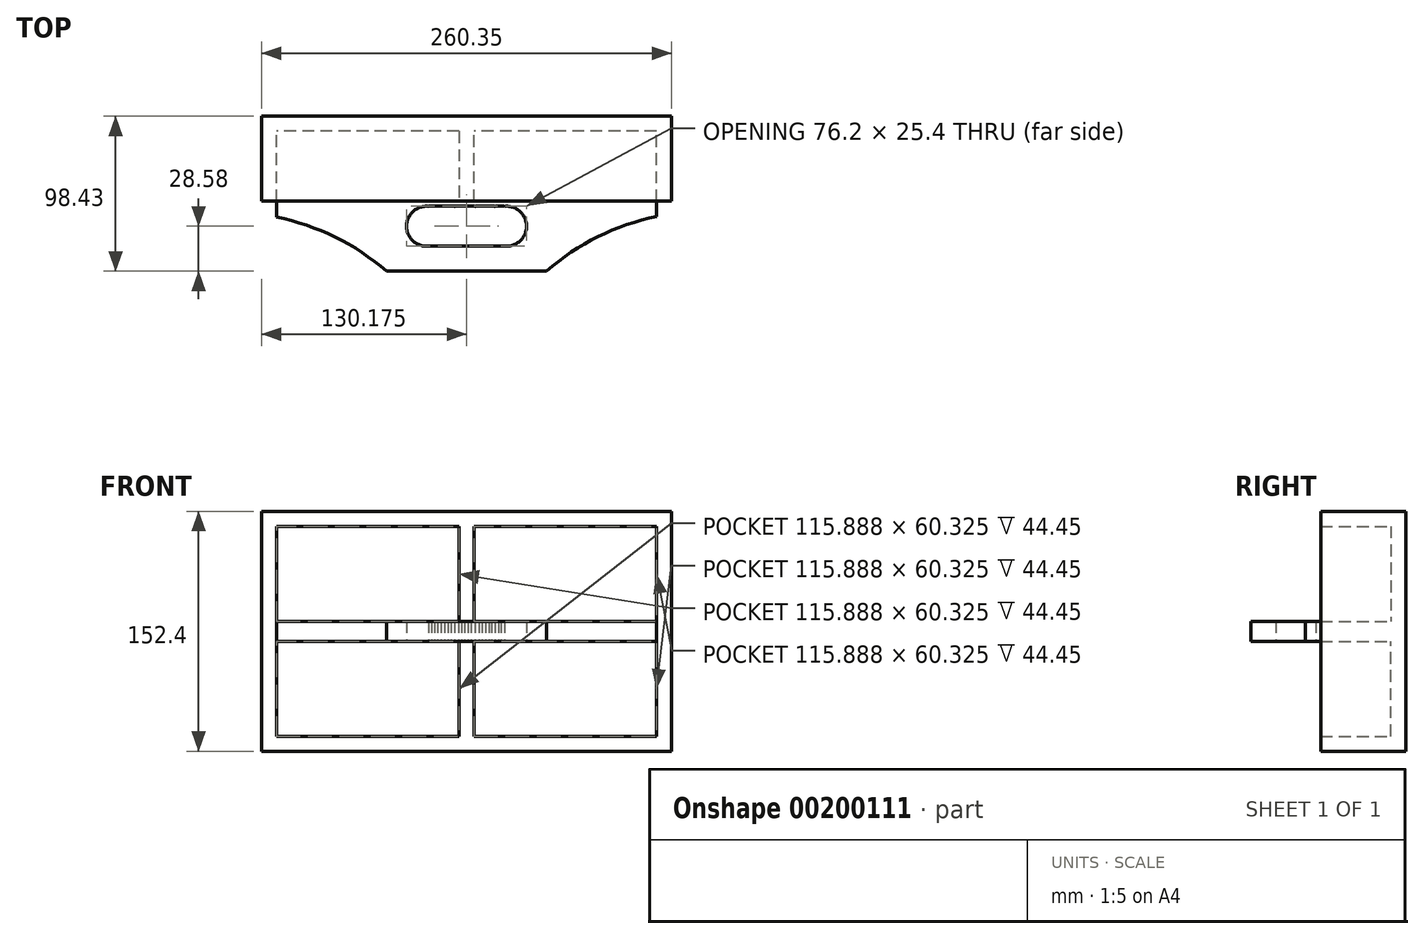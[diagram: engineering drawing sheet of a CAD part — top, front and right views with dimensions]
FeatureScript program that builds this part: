
annotation { "Feature Type Name" : "Feature", "Feature Type Description" : "" }
export const myFeature = defineFeature(function(context is Context, id is Id, definition is map)
    precondition{}
    {
        {
            var Q0;
            Q0=qCreatedBy(makeId("Front.planeOp"),FACE);
            var sketch = newSketch(context, id + "F0", { "sketchPlane" : qUnion([Q0])});
            skLineSegment(sketch, "E0", {"start": v(-126.24, -36.22) * mm, "end": v(134.1, -36.22) * mm});
            skLineSegment(sketch, "E1", {"start": v(134.1, -36.22) * mm, "end": v(134.1, 116.18) * mm});
            skLineSegment(sketch, "E2", {"start": v(134.1, 116.18) * mm, "end": v(-126.24, 116.18) * mm});
            skLineSegment(sketch, "E3", {"start": v(-126.24, -36.22) * mm, "end": v(-126.24, 116.18) * mm});
            skSolve(sketch);
        }
        {
            var Q0;
            Q0=makeQuery(id+"F0.imprint","IMPRINT",FACE,{"disambiguationData":[TD([[makeQuery(id+"F0.imprint","IMPRINT",EDGE,{"derivedFrom":sQuery(id+"F0.wireOp",EDGE,"E0")}),1.0]])]});
            extrude(context, id + "F1", {"entities" : qUnion([Q0]), "depth" : 9.52 * mm});
        }
        {
            var Q0;
            Q0=makeQuery(id+"F1.opExtrude","CAP_FACE",FACE,{"disambiguationData":[OSD([sQuery(id+"F0.wireOp",EDGE,"E0"),sQuery(id+"F0.wireOp",EDGE,"E1"),sQuery(id+"F0.wireOp",EDGE,"E2"),sQuery(id+"F0.wireOp",EDGE,"E3")])],"isStart":false});
            var sketch = newSketch(context, id + "F2", { "sketchPlane" : qUnion([Q0])});
            skLineSegment(sketch, "E4", {"start": v(134.1, -36.22) * mm, "end": v(134.1, -26.7) * mm});
            skLineSegment(sketch, "E5", {"start": v(-126.24, -36.22) * mm, "end": v(-126.24, -26.7) * mm});
            skLineSegment(sketch, "E6", {"start": v(-126.24, 116.18) * mm, "end": v(-126.24, 106.65) * mm});
            skLineSegment(sketch, "E7", {"start": v(134.1, 116.18) * mm, "end": v(134.1, 106.65) * mm});
            skLineSegment(sketch, "E8", {"start": v(-126.24, 106.65) * mm, "end": v(134.1, 106.65) * mm});
            skLineSegment(sketch, "E9", {"start": v(-126.24, -26.7) * mm, "end": v(134.1, -26.7) * mm});
            skLineSegment(sketch, "E10", {"start": v(124.58, 65.45) * mm, "end": v(124.58, 106.65) * mm});
            skLineSegment(sketch, "E11", {"start": v(124.58, 65.45) * mm, "end": v(124.58, -26.7) * mm});
            skLineSegment(sketch, "E12", {"start": v(-116.72, 49.02) * mm, "end": v(-116.72, 106.65) * mm});
            skLineSegment(sketch, "E13", {"start": v(-116.72, 49.02) * mm, "end": v(-116.72, -26.7) * mm});
            skLineSegment(sketch, "E14", {"start": v(-0.83, 77.84) * mm, "end": v(-0.83, 106.65) * mm});
            skLineSegment(sketch, "E15", {"start": v(-0.83, 77.84) * mm, "end": v(-0.83, -26.7) * mm});
            skLineSegment(sketch, "E16", {"start": v(8.7, 55.01) * mm, "end": v(8.7, 106.65) * mm});
            skLineSegment(sketch, "E17", {"start": v(8.7, 55.01) * mm, "end": v(8.7, -26.7) * mm});
            skPoint(sketch, "E18.start.orphan", {"position": v(-116.72, 77.84) * mm});
            skSolve(sketch);
        }
        {
            var Q0;
            {var subQ1=sQuery(id+"F2.wireOp",EDGE,"E12");Q0=makeQuery(id+"F2.imprint","IMPRINT",FACE,{"disambiguationData":[TD([[makeQuery(id+"F2.imprint","IMPRINT",EDGE,{"derivedFrom":subQ1}),1.0]])]});}
            var Q1;
            {var subQ3=sQuery(id+"F2.wireOp",EDGE,"E6");Q1=makeQuery(id+"F2.imprint","IMPRINT",FACE,{"disambiguationData":[TD([[makeQuery(id+"F2.imprint","IMPRINT",EDGE,{"derivedFrom":subQ3}),-1.0]])]});}
            var Q2;
            {var subQ1=sQuery(id+"F2.wireOp",EDGE,"E14");Q2=makeQuery(id+"F2.imprint","IMPRINT",FACE,{"disambiguationData":[TD([[makeQuery(id+"F2.imprint","IMPRINT",EDGE,{"derivedFrom":subQ1}),-1.0]])]});}
            var Q3;
            {var subQ1=sQuery(id+"F2.wireOp",EDGE,"E10");Q3=makeQuery(id+"F2.imprint","IMPRINT",FACE,{"disambiguationData":[TD([[makeQuery(id+"F2.imprint","IMPRINT",EDGE,{"derivedFrom":subQ1}),-1.0]])]});}
            var Q4;
            {var subQ4=sQuery(id+"F2.wireOp",EDGE,"E4");Q4=makeQuery(id+"F2.imprint","IMPRINT",FACE,{"disambiguationData":[TD([[makeQuery(id+"F2.imprint","IMPRINT",EDGE,{"derivedFrom":subQ4}),1.0]])]});}
            extrude(context, id + "F3", {"entities" : qUnion([Q0, Q1, Q2, Q3, Q4]), "operationType" : NewBodyOperationType.ADD, "depth" : 44.45 * mm});
        }
        {
            var Q0;
            {var subQ0=sQuery(id+"F2.wireOp",EDGE,"E10");var subQ3=sQuery(id+"F2.wireOp",EDGE,"E11");Q0=makeQuery(id+"F3.boolean.opBoolean","SPLIT",FACE,{"disambiguationData":[TD([makeQuery(id+"F3.opExtrude","SWEPT_FACE",FACE,{"disambiguationData":[OSD([subQ0,subQ3])]})])],"derivedFrom":makeQuery(id+"F1.opExtrude","CAP_FACE",FACE,{"disambiguationData":[OSD([sQuery(id+"F0.wireOp",EDGE,"E0"),sQuery(id+"F0.wireOp",EDGE,"E1"),sQuery(id+"F0.wireOp",EDGE,"E2"),sQuery(id+"F0.wireOp",EDGE,"E3")])],"isStart":false})});}
            var sketch = newSketch(context, id + "F4", { "sketchPlane" : qUnion([Q0])});
            skPoint(sketch, "E19.end.orphan", {"position": v(-116.72, 35.97) * mm});
            skPoint(sketch, "E19.start.orphan", {"position": v(124.58, 35.97) * mm});
            skLineSegment(sketch, "E20", {"start": v(38.58, 33.63) * mm, "end": v(124.58, 33.63) * mm});
            skLineSegment(sketch, "E21", {"start": v(38.58, 33.63) * mm, "end": v(-116.72, 33.63) * mm});
            skLineSegment(sketch, "E22", {"start": v(37.81, 46.33) * mm, "end": v(124.58, 46.33) * mm});
            skLineSegment(sketch, "E23", {"start": v(-4.04, 46.33) * mm, "end": v(-116.72, 46.33) * mm});
            skPoint(sketch, "E24", {"position": v(-4.04, 46.33) * mm});
            skLineSegment(sketch, "E25", {"start": v(-116.72, 46.33) * mm, "end": v(-116.72, 33.63) * mm});
            skLineSegment(sketch, "E26", {"start": v(124.58, 33.63) * mm, "end": v(124.58, 46.33) * mm});
            skLineSegment(sketch, "E27", {"start": v(37.81, 46.33) * mm, "end": v(-4.04, 46.33) * mm});
            skSolve(sketch);
        }
        {
            var Q0;
            {var subQ1=sQuery(id+"F4.wireOp",EDGE,"E23");Q0=makeQuery(id+"F4.imprint","IMPRINT",FACE,{"disambiguationData":[TD([[makeQuery(id+"F4.imprint","IMPRINT",EDGE,{"derivedFrom":subQ1}),1.0]])]});}
            var Q1;
            {var subQ2=sQuery(id+"F4.wireOp",EDGE,"E20");Q1=makeQuery(id+"F4.imprint","IMPRINT",FACE,{"disambiguationData":[TD([[makeQuery(id+"F4.imprint","IMPRINT",EDGE,{"derivedFrom":subQ2}),1.0]])]});}
            extrude(context, id + "F5", {"entities" : qUnion([Q0, Q1]), "operationType" : NewBodyOperationType.ADD, "depth" : 88.9 * mm});
        }
        {
            var Q0;
            Q0=makeQuery(id+"F5.opExtrude","SWEPT_FACE",FACE,{"disambiguationData":[OSD([sQuery(id+"F4.wireOp",EDGE,"E20"),sQuery(id+"F4.wireOp",EDGE,"E21")])]});
            var sketch = newSketch(context, id + "F6", { "sketchPlane" : qUnion([Q0])});
            skLineSegment(sketch, "E28", {"start": v(-47.37, 98.43) * mm, "end": v(-21.47, 98.43) * mm});
            skLineSegment(sketch, "E29", {"start": v(54.73, 98.43) * mm, "end": v(29.33, 98.43) * mm});
            skPoint(sketch, "E30.end.orphan", {"position": v(29.33, 69.85) * mm});
            skPoint(sketch, "E30.start.orphan", {"position": v(29.33, 96.52) * mm});
            skLineSegment(sketch, "E31", {"start": v(29.33, 98.43) * mm, "end": v(29.33, 96.52) * mm});
            skArc(sketch, "E32", {"start": v(-21.47, 82.55) * mm, "mid": v(-34.17, 69.85) * mm, "end": v(-21.47, 57.15) * mm});
            skArc(sketch, "E33", {"start": v(29.33, 57.15) * mm, "mid": v(42.03, 69.85) * mm, "end": v(29.33, 82.55) * mm});
            skLineSegment(sketch, "E34", {"start": v(-21.47, 57.15) * mm, "end": v(29.33, 57.15) * mm});
            skLineSegment(sketch, "E35", {"start": v(29.33, 82.55) * mm, "end": v(-21.47, 82.55) * mm});
            skArc(sketch, "E36", {"start": v(-116.72, 63.5) * mm, "mid": v(-79.78, 76.47) * mm, "end": v(-47.37, 98.42) * mm});
            skArc(sketch, "E37", {"start": v(54.73, 98.43) * mm, "mid": v(87.42, 76.64) * mm, "end": v(124.58, 63.94) * mm});
            skLineSegment(sketch, "E38", {"start": v(-21.47, 69.85) * mm, "end": v(29.33, 69.85) * mm});
            skPoint(sketch, "E39", {"position": v(-19.25, 69.85) * mm});
            skPoint(sketch, "E40", {"position": v(-17.28, 69.85) * mm});
            skPoint(sketch, "E41", {"position": v(-15.5, 69.85) * mm});
            skPoint(sketch, "E42", {"position": v(-13.25, 69.85) * mm});
            skPoint(sketch, "E43", {"position": v(-11.23, 69.85) * mm});
            skPoint(sketch, "E44", {"position": v(-8.84, 69.85) * mm});
            skPoint(sketch, "E45", {"position": v(-6.77, 69.85) * mm});
            skPoint(sketch, "E46", {"position": v(-4.8, 69.85) * mm});
            skPoint(sketch, "E47", {"position": v(-2.3, 69.85) * mm});
            skPoint(sketch, "E48", {"position": v(-0.29, 69.85) * mm});
            skPoint(sketch, "E49", {"position": v(1.63, 69.85) * mm});
            skPoint(sketch, "E50", {"position": v(3.93, 69.85) * mm});
            skPoint(sketch, "E51", {"position": v(5.8, 69.85) * mm});
            skPoint(sketch, "E52", {"position": v(8.06, 69.85) * mm});
            skPoint(sketch, "E53", {"position": v(10.69, 69.85) * mm});
            skPoint(sketch, "E54", {"position": v(12.84, 69.85) * mm});
            skPoint(sketch, "E55", {"position": v(14.86, 69.85) * mm});
            skPoint(sketch, "E56", {"position": v(17.06, 69.85) * mm});
            skPoint(sketch, "E57", {"position": v(19.22, 69.85) * mm});
            skPoint(sketch, "E58", {"position": v(20.68, 69.85) * mm});
            skPoint(sketch, "E59", {"position": v(23.26, 69.85) * mm});
            skPoint(sketch, "E60", {"position": v(25.04, 69.85) * mm});
            skPoint(sketch, "E61", {"position": v(26.87, 69.85) * mm});
            skSolve(sketch);
        }
        {
            var Q0;
            Q0=sQuery(id+"F6.wireOp",VERTEX,"E38.start");
            var Q1;
            Q1=sQuery(id+"F6.wireOp",VERTEX,"E39");
            var Q2;
            Q2=sQuery(id+"F6.wireOp",VERTEX,"E40");
            var Q3;
            Q3=sQuery(id+"F6.wireOp",VERTEX,"E41");
            var Q4;
            Q4=sQuery(id+"F6.wireOp",VERTEX,"E42");
            var Q5;
            Q5=sQuery(id+"F6.wireOp",VERTEX,"E43");
            var Q6;
            Q6=sQuery(id+"F6.wireOp",VERTEX,"E44");
            var Q7;
            Q7=sQuery(id+"F6.wireOp",VERTEX,"E45");
            var Q8;
            Q8=sQuery(id+"F6.wireOp",VERTEX,"E46");
            var Q9;
            Q9=sQuery(id+"F6.wireOp",VERTEX,"E47");
            var Q10;
            Q10=sQuery(id+"F6.wireOp",VERTEX,"E48");
            var Q11;
            Q11=sQuery(id+"F6.wireOp",VERTEX,"E49");
            var Q12;
            Q12=sQuery(id+"F6.wireOp",VERTEX,"E50");
            var Q13;
            Q13=sQuery(id+"F6.wireOp",VERTEX,"E51");
            var Q14;
            Q14=sQuery(id+"F6.wireOp",VERTEX,"E52");
            var Q15;
            Q15=sQuery(id+"F6.wireOp",VERTEX,"E53");
            var Q16;
            Q16=sQuery(id+"F6.wireOp",VERTEX,"E54");
            var Q17;
            Q17=sQuery(id+"F6.wireOp",VERTEX,"E55");
            var Q18;
            Q18=sQuery(id+"F6.wireOp",VERTEX,"E56");
            var Q19;
            Q19=sQuery(id+"F6.wireOp",VERTEX,"E57");
            var Q20;
            Q20=sQuery(id+"F6.wireOp",VERTEX,"E58");
            var Q21;
            Q21=sQuery(id+"F6.wireOp",VERTEX,"E59");
            var Q22;
            Q22=sQuery(id+"F6.wireOp",VERTEX,"E60");
            var Q23;
            Q23=sQuery(id+"F6.wireOp",VERTEX,"E61");
            var Q24;
            Q24=sQuery(id+"F6.wireOp",VERTEX,"E30.end.orphan");
            var Q25;
            Q25=makeQuery(id+"F1.opExtrude","SWEPT_BODY",BODY,{"disambiguationData":[OSD([sQuery(id+"F0.wireOp",EDGE,"E0"),sQuery(id+"F0.wireOp",EDGE,"E1"),sQuery(id+"F0.wireOp",EDGE,"E2"),sQuery(id+"F0.wireOp",EDGE,"E3")])]});
            hole(context, id + "F7", {"style" : HoleStyle.SIMPLE, "endStyle" : HoleEndStyle.THROUGH, "holeDiameter" : 25.4 * mm, "locations" : qUnion([Q0, Q1, Q2, Q3, Q4, Q5, Q6, Q7, Q8, Q9, Q10, Q11, Q12, Q13, Q14, Q15, Q16, Q17, Q18, Q19, Q20, Q21, Q22, Q23, Q24]), "scope" : qUnion([Q25]), "isTappedThrough" : true});
        }
        {
            var Q0;
            Q0=makeQuery(id+"F5.opExtrude","SWEPT_FACE",FACE,{"disambiguationData":[OSD([sQuery(id+"F4.wireOp",EDGE,"E20"),sQuery(id+"F4.wireOp",EDGE,"E21")])]});
            var sketch = newSketch(context, id + "F8", { "sketchPlane" : qUnion([Q0])});
            skPoint(sketch, "E62", {"position": v(124.58, 63.71) * mm});
            skPoint(sketch, "E63", {"position": v(-116.72, 64.06) * mm});
            skPoint(sketch, "E64", {"position": v(-116.72, 98.43) * mm});
            skPoint(sketch, "E65", {"position": v(124.58, 98.43) * mm});
            skPoint(sketch, "E66", {"position": v(-46.87, 98.43) * mm});
            skPoint(sketch, "E67", {"position": v(54.73, 98.43) * mm});
            skArc(sketch, "E68", {"start": v(-116.72, 64.06) * mm, "mid": v(-79.56, 76.7) * mm, "end": v(-46.87, 98.43) * mm});
            skArc(sketch, "E69", {"start": v(54.73, 98.42) * mm, "mid": v(87.4, 76.52) * mm, "end": v(124.58, 63.71) * mm});
            skPoint(sketch, "E70.start.orphan", {"position": v(124.58, 76.2) * mm});
            skSolve(sketch);
        }
        {
            var Q0;
            {var subQ0=sQuery(id+"F8.wireOp",EDGE,"E68");Q0=makeQuery(id+"F8.imprint","IMPRINT",FACE,{"disambiguationData":[TD([[makeQuery(id+"F8.imprint","IMPRINT",EDGE,{"derivedFrom":subQ0}),1.0]])]});}
            var Q1;
            {var subQ0=sQuery(id+"F8.wireOp",EDGE,"E69");Q1=makeQuery(id+"F8.imprint","IMPRINT",FACE,{"disambiguationData":[TD([[makeQuery(id+"F8.imprint","IMPRINT",EDGE,{"derivedFrom":subQ0}),1.0]])]});}
            extrude(context, id + "F9", {"entities" : qUnion([Q0, Q1]), "operationType" : NewBodyOperationType.REMOVE, "oppositeDirection" : true, "depth" : 25.4 * mm});
        }
    });
